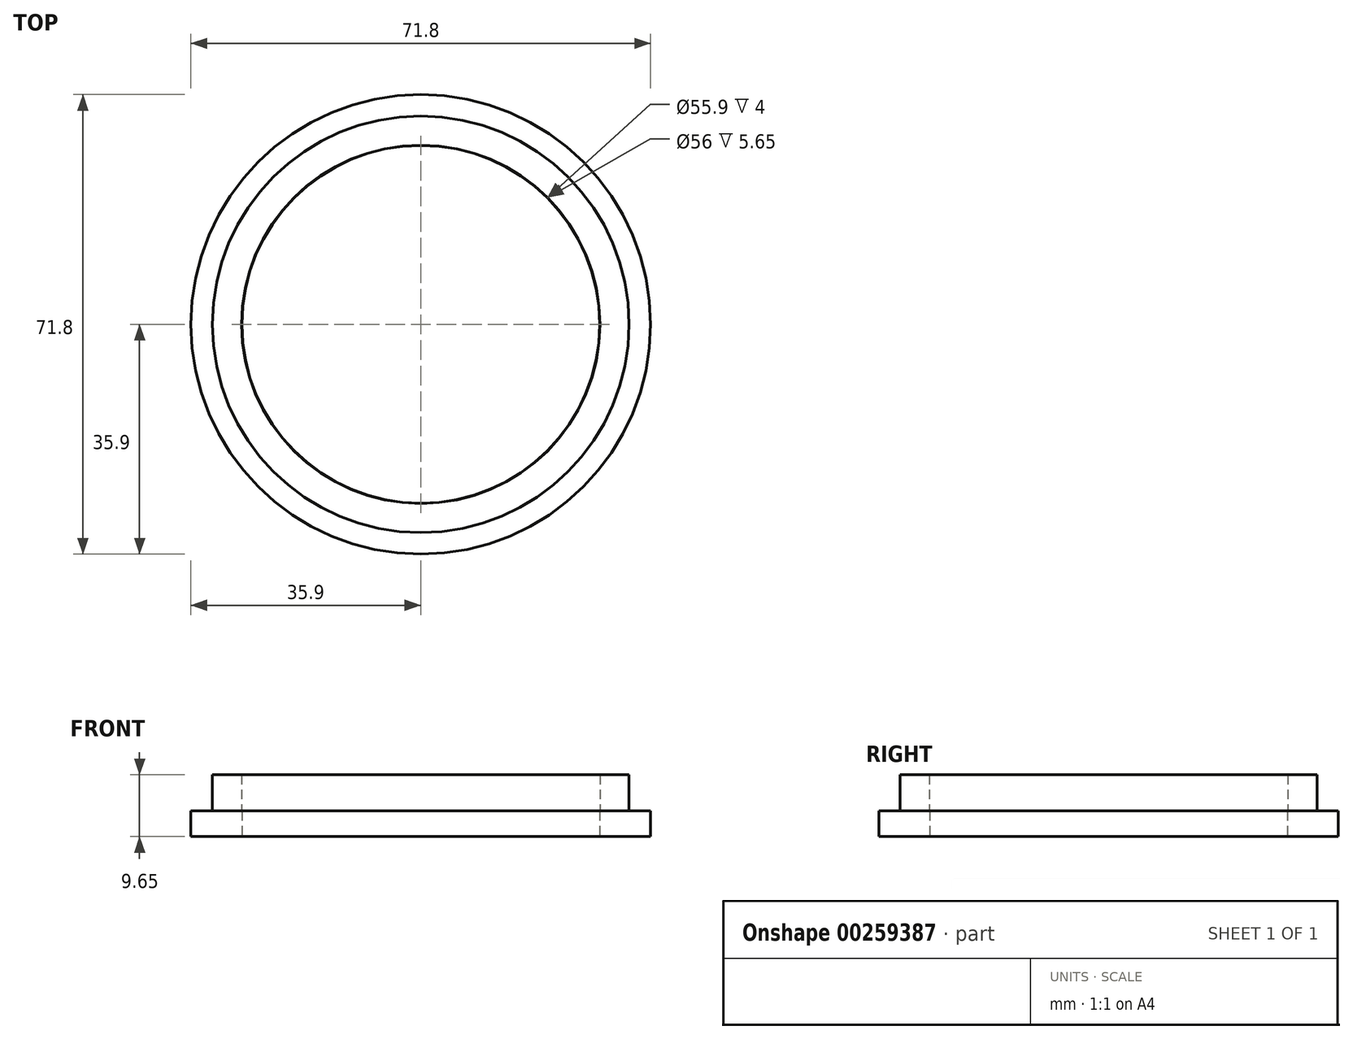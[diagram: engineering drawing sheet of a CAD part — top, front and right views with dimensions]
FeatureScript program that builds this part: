
annotation { "Feature Type Name" : "Feature", "Feature Type Description" : "" }
export const myFeature = defineFeature(function(context is Context, id is Id, definition is map)
    precondition{}
    {
        {
            var Q0;
            Q0=qCreatedBy(makeId("Top.planeOp"),FACE);
            var sketch = newSketch(context, id + "F0", { "sketchPlane" : qUnion([Q0])});
            skCircle(sketch, "E0", {"center": v(0, 0) * mm, "radius": 27.95 * mm});
            skCircle(sketch, "E1.0.0", {"center": v(0, 0) * mm, "radius": 35.9 * mm});
            skSolve(sketch);
        }
        {
            var Q0;
            Q0=qSketchRegion(id+"F0",true);
            extrude(context, id + "F1", {"entities" : qUnion([Q0]), "depth" : 4 * mm});
        }
        {
            var Q0;
            Q0=makeQuery(id+"F1.opExtrude","CAP_FACE",FACE,{"disambiguationData":[OSD([sQuery(id+"F0.wireOp",EDGE,"E1.0.0")])],"isStart":false});
            var sketch = newSketch(context, id + "F2", { "sketchPlane" : qUnion([Q0])});
            skCircle(sketch, "E2", {"center": v(0, 0) * mm, "radius": 28 * mm});
            skCircle(sketch, "E3", {"center": v(0, 0) * mm, "radius": 32.55 * mm});
            skSolve(sketch);
        }
        {
            var Q0;
            Q0=makeQuery(id+"F2.imprint","IMPRINT",FACE,{"disambiguationData":[TD([[makeQuery(id+"F2.imprint","IMPRINT",EDGE,{"derivedFrom":sQuery(id+"F2.wireOp",EDGE,"E2")}),-1.0]])]});
            extrude(context, id + "F3", {"entities" : qUnion([Q0]), "operationType" : NewBodyOperationType.ADD, "depth" : 5.65 * mm});
        }
    });
